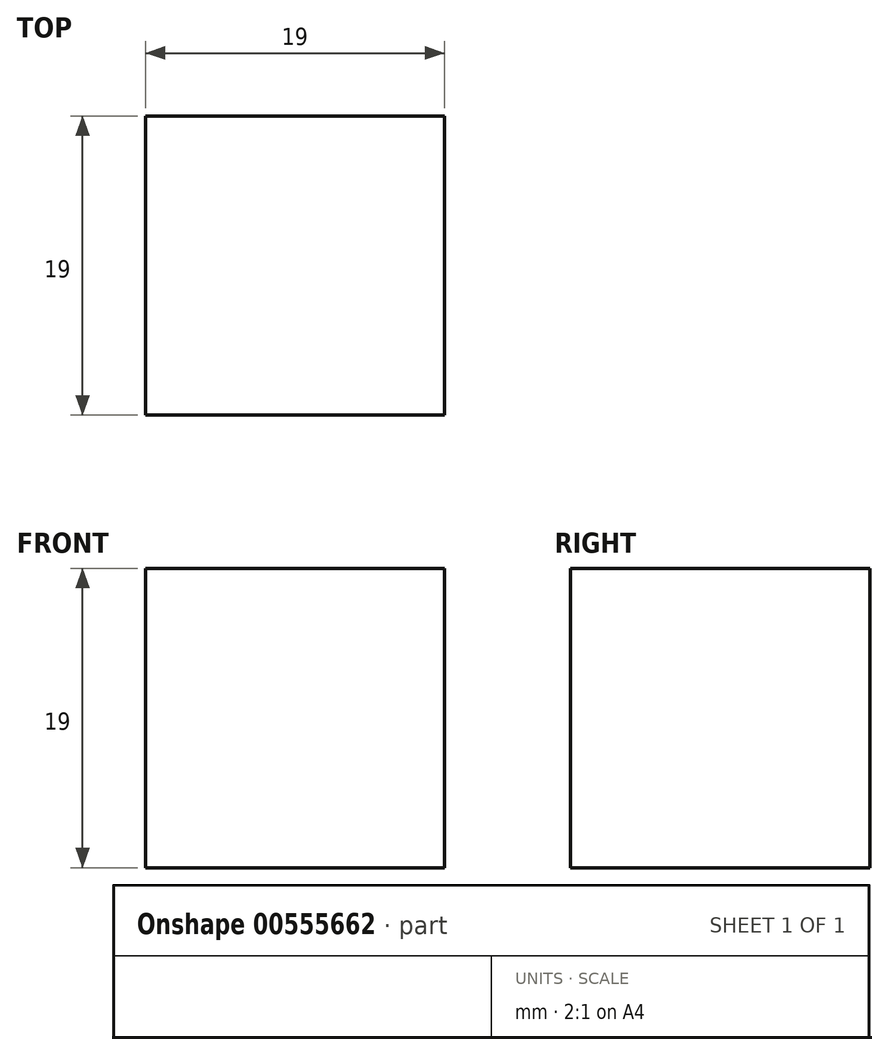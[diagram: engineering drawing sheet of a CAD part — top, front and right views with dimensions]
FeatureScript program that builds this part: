
annotation { "Feature Type Name" : "Feature", "Feature Type Description" : "" }
export const myFeature = defineFeature(function(context is Context, id is Id, definition is map)
    precondition{}
    {
        {
            var Q0;
            Q0=qCreatedBy(makeId("Top.planeOp"),FACE);
            var sketch = newSketch(context, id + "F0", { "sketchPlane" : qUnion([Q0])});
            skLineSegment(sketch, "E0.bottom", {"start": v(9.5, 9.5) * mm, "end": v(-9.5, 9.5) * mm});
            skLineSegment(sketch, "E0.top", {"start": v(9.5, -9.5) * mm, "end": v(-9.5, -9.5) * mm});
            skLineSegment(sketch, "E0.left", {"start": v(9.5, 9.5) * mm, "end": v(9.5, -9.5) * mm});
            skLineSegment(sketch, "E0.right", {"start": v(-9.5, 9.5) * mm, "end": v(-9.5, -9.5) * mm});
            skPoint(sketch, "E0.middle", {"position": v(0, 0) * mm});
            skSolve(sketch);
        }
        {
            var Q0;
            Q0=makeQuery(id+"F0.imprint","IMPRINT",FACE,{"disambiguationData":[TD([[makeQuery(id+"F0.imprint","IMPRINT",EDGE,{"derivedFrom":sQuery(id+"F0.wireOp",EDGE,"E0.bottom")}),1.0]])]});
            extrude(context, id + "F1", {"entities" : qUnion([Q0]), "depth" : 19 * mm, "offsetDistance" : 25.4 * mm});
        }
    });
